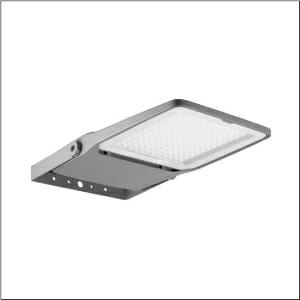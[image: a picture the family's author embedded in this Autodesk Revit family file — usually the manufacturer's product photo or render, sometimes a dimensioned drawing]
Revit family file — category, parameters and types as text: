
# Revit family: floodlight_fl_20_midi___pl61_5xa7682d3c2ac_39fc
name_source: partatom
category: Lighting Fixtures
units: mm (PartAtom-declared; Revit-internal decimal feet)

## family parameters
Cut with Voids When Loaded = No
Host = Face
Light Source = No
Part Type = Normal
Room Calculation Point = No
Round Connector Dimension = Use Diameter
Shared = No

## types (1)
- --- (1 x LED 5000K / CRI = 70 (unbekannt), 18470 lm, 5000K)
    Apparent Load = 142 VA
    CIE Flux Codes = 33 65 98 100 100
    Color Rendering = 70
    Color Temperature = 5000K
    Default Elevation = 1800 mm
    Description = Floodlight FL 20 midi, floodlight, primary light control with lens, of plastic, primary optical cover: protective disc, of toughened safety glass, transparent, light distribution: PL61, light emission: direct distribution, primary light characteristic: asymmetric, installation type: surface-mounted, LED, High Power LED, rated luminous flux: 18.470lm, luminous efficacy: 130lm/W, light colour: 750, colour temperature: 5000K, control gear: ECG Plus, control: digital communication interface, time-dependent luminous flux control, flexible luminous flux parameterisation, power reduction, overheat protection, electronic power reduction, with terminal, 5-pole, max. 2.5mm², mains connection: 220..240V, AC, 50/60Hz, rated input power: 142W, LED unit, of diecast aluminium, powder-coated, Siteco® metallic grey (DB 702S), corrosivity category C5 mid according to DIN EN ISO 12944, incl. 1x M20 cable gland for cable Ø 6.5..12mm, length: 731mm, width: 450mm, height: 76mm, housing frame, of diecast aluminium, powder-coated, Siteco® metallic grey (DB 702S), wall fastening, of steel, powder-coated, Siteco® metallic grey (DB 702S), DALI, protection rating (complete): IP66, insulation class (complete): insulation class II (safety insulation), certification: CE, ENEC, VDE, protection symbol: D, permissible operating ambient temperature: -40..+40°C, permissible operating ambient temperature for outdoor applications: -40..+50°C, standard: DIN EN 12944, packaging unit: 1 piece

Light Distribution: PL61
    Height = 76 mm
    Lamp = 1 x LED 5000K / CRI >= 70 (unbekannt)
    Lamp Light Flux = 18470 lm
    Lamp count = 1
    Length = 731 mm
    Luminous efficacy = 130 lm/W
    Manufacturer = Siteco
    ModVariant = No
    Model = 5XA7682D3C2AC
    Mounting Place = Wall
    Mounting Type = Surface mounted
    Number of Poles = 1
    OnlyDefault = Yes
    Power Factor = 1
    Product Name = Floodlight FL 20 midi | PL61
    Product group = floodlight | wall mounted
    ProductGroupID = 2001
    Protection Class = Protection class II
    Protection Degree = IP 66
    RLX_Detail_Level = 1
    RLX_Emergency_Light_Flux = 0 lm
    RLX_Emergency_Type = 0
    RLX_Emergency_Type_DB = No
    RlxData = <blob elided: 92325 chars, md5=841ca27a>
    Socket = socket
    Standby Power = 0 W
    System Light Flux = 18470 lm
    System Power = 142 W
    Type Comments = factory setting: luminous flux: 100 % | dim-lin: 254 | 489 mA
    Type Image = l_1005944.jpg
    URL = http://relux.com
    VarID = @adj_147135
    Voltage = 0 V
    Weight = 0.00 kg
    Width = 450 mm

## geometry (parser evidence)
native form markers: Blend x4, Sweep x15
no freeform markers — native parametric forms only
